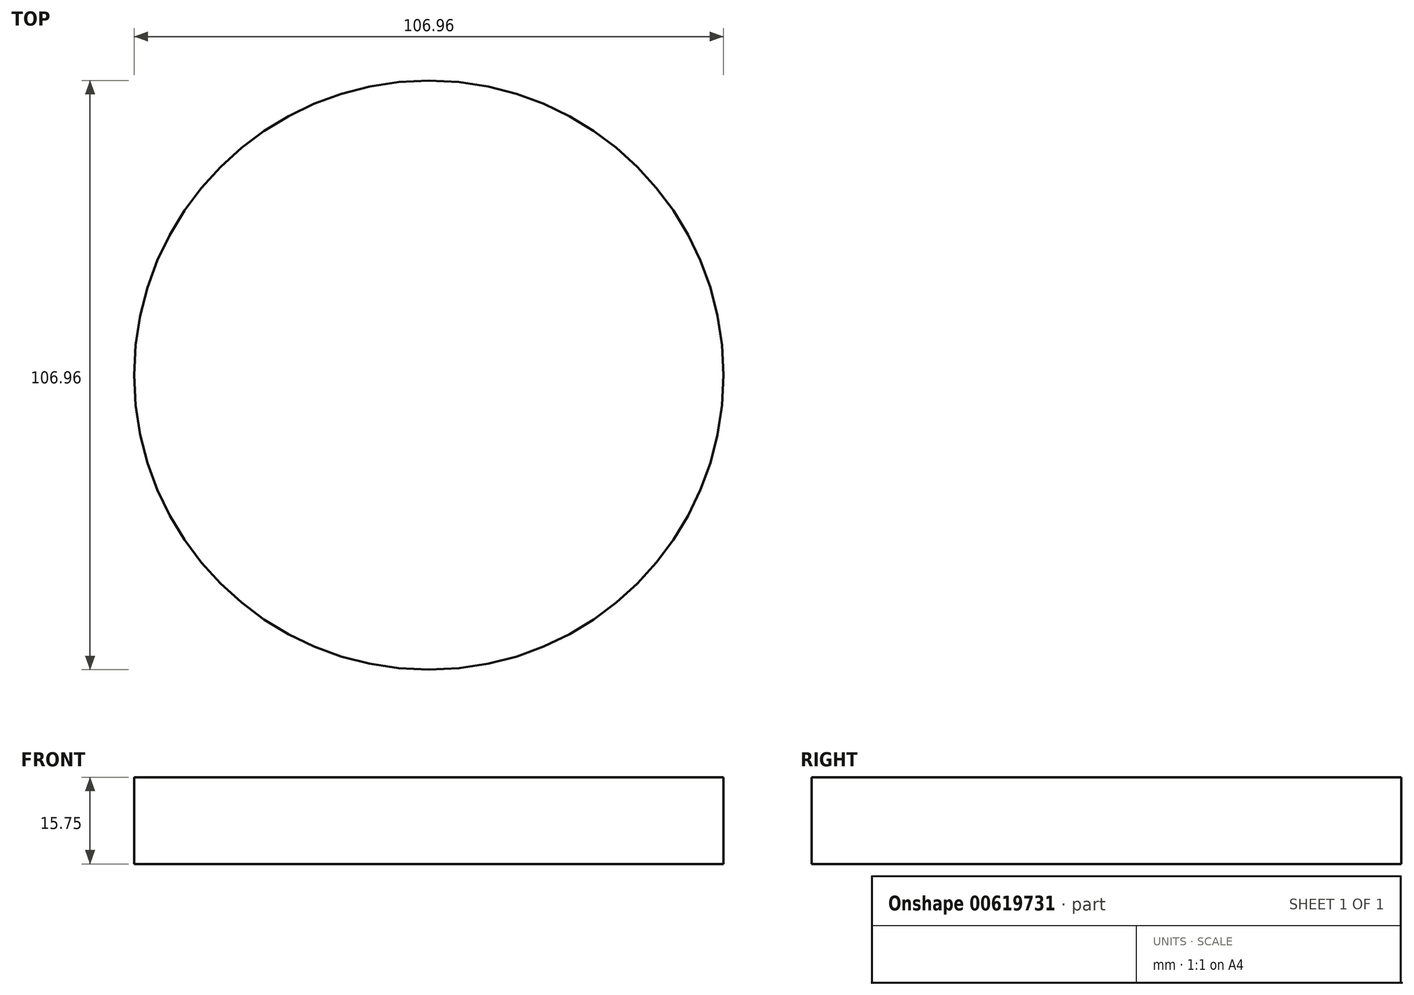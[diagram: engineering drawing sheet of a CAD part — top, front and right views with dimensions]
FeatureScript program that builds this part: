
annotation { "Feature Type Name" : "Feature", "Feature Type Description" : "" }
export const myFeature = defineFeature(function(context is Context, id is Id, definition is map)
    precondition{}
    {
        {
            var Q0;
            Q0=qCreatedBy(makeId("Top.planeOp"),FACE);
            var sketch = newSketch(context, id + "F0", { "sketchPlane" : qUnion([Q0])});
            skCircle(sketch, "E0", {"center": v(0, 0) * mm, "radius": 53.48 * mm});
            skSolve(sketch);
        }
        {
            var Q0;
            Q0 = qSketchRegion(id + "F0", true);
            extrude(context, id + "F1", {"entities" : qUnion([Q0]), "depth" : 15.75 * mm, "offsetDistance" : 25.4 * mm});
        }
    });
